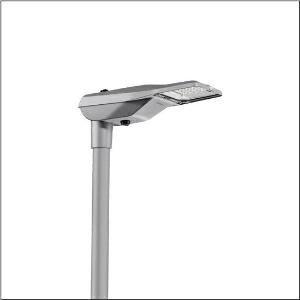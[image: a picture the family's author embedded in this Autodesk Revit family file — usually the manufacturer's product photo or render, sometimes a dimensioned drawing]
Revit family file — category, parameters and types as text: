
# Revit family: streetlight_sl_21_micro___st0_8a_5xe1c33t08db_e381
name_source: partatom
category: Lighting Fixtures
units: mm (PartAtom-declared; Revit-internal decimal feet)

## family parameters
Cut with Voids When Loaded = No
Host = Face
Light Source = No
Part Type = Normal
Room Calculation Point = No
Round Connector Dimension = Use Diameter
Shared = No

## types (1)
- --- (1 x LED, 5110 lm, 39.1 W, 3000K)
    Apparent Load = 39 VA
    CIE Flux Codes = 38 75 97 100 100
    Color Rendering = 70
    Color Temperature = 3000K
    Default Elevation = 1800 mm
    Description = Streetlight SL 21 micro, mast luminaire, primary light control with lens, of PMMA, primary optical cover: cover, of toughened safety glass, transparent, light distribution: ST0.8a, light emission: direct distribution, primary light characteristic: asymmetric, installation type: side-entry, post-top, LED, High Power LED, rated luminous flux: 5.110lm, luminous efficacy: 131lm/W, light colour: 730, colour temperature: 3000K, control: flexible luminous flux parameterisation, time-dependent luminous flux control, constant luminous flux control, overheat protection, presetting dimming logarithmic, mains connection: 220..240V, AC, 50/60Hz, start of lifetime: 39W, end of service life: 41W, reduction: 18W, luminaire housing, of diecast aluminium, powder-coated, Siteco® metallic grey (DB 702S), corrosivity category C5 mid according to DIN EN ISO 12944, please order mast flange separately, inclination adjustable: 0°, 5°, 10°, 15°, sealing non-destructively replaceable, multi-level sealing system, length: 528mm, width: 235mm, height: 110mm, mast flange for spigot size: 42mm (side-entry): 5XC10008XM4, 60/48mm (side-entry/post-top): 5XC10108XM2, 76/60mm (side-entry/post-top): 5XC10108XM1, Smart Interface below and above, protection rating (complete): IP66, insulation class (complete): insulation class II (safety insulation), certification: CE, ENEC, ENEC+, VDE, impact resistance: IK09, permissible operating ambient temperature for outdoor applications: -40..+50°C, standard-compliant lighting for roads and squares, packaging unit: 1 piece

Light Distribution: ST0.8a
    Height = 110 mm
    Lamp = 1 x LED
    Lamp Light Flux = 5110 lm
    Lamp Power = 39.1 W
    Lamp count = 1
    Length = 528 mm
    Luminous efficacy = 131 lm/W
    Manufacturer = Siteco
    ModVariant = No
    Model = 5XE1C33T08DB
    Number of Poles = 1
    OnlyDefault = Yes
    Power Factor = 1
    Product Name = Streetlight SL 21 micro | ST0.8a
    Product group = mast luminaire | pylon top
    ProductGroupID = 6100
    Protection Class = Protection class II
    Protection Degree = IP 66
    RLX_Detail_Level = 1
    RLX_Emergency_Light_Flux = 0 lm
    RLX_Emergency_Type = 0
    RLX_Emergency_Type_DB = No
    RlxData = <blob elided: 98513 chars, md5=6a14b036>
    Socket = socket
    Standby Power = 0 W
    System Light Flux = 5110 lm
    System Power = 39 W
    Type Comments = factory setting: luminous flux: 100 % | dim-lin: 254 | 765 mA
    Type Image = l_1007239.jpg
    URL = http://relux.com
    VarID = @adj_104507
    Voltage = 0 V
    Weight = 0.00 kg
    Width = 235 mm

## geometry (parser evidence)
native form markers: Blend x4, Sweep x10
no freeform markers — native parametric forms only
